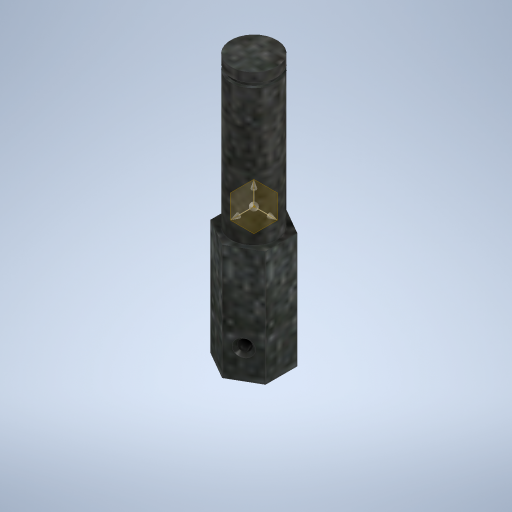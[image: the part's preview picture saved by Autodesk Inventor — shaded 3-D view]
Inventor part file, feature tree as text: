
AUTODESK INVENTOR PART (.ipt)
format: ipt  version: 2023 (Build 270158030, 158C)  size: 348,160 bytes
history: native  units: in
note: dims shown in document units (in); Inventor stores cm internally (conversion verified against a paired STEP export)
features: sketch x5, extrude x3, hole x1, revolve x1
ambient origin geometry x8: Origin, YZ Plane, XZ Plane, XY Plane, X Axis, Y Axis, Z Axis, Center Point
bodies: Solid1 (feature_tree)
feature tree (10):
  extrude  "Extrusion1"  Depth=0.7874in TaperAngle=0.0deg
  extrude  "Extrusion2"  Depth=0.1969in TaperAngle=0.0deg
  hole  "Hole1"  [1 undecoded]
  extrude  "Extrusion4"  Depth=0.1083in
  revolve  "Revolution1"  [1 undecoded]
  sketch  "Sketch1"  dims[d0=0.375in d1=0.7874in d2=0.0in]
  sketch  "Sketch2"  dims[d3=0.315in d4=0.1969in d5=0.0in]
  sketch  "Sketch4"  dims[d11=0.835in d12=0.0in d13=0.1969in]
  sketch  "Sketch5"  dims[d14=0.0787in d15=0.75in d16=0.1181in d17=0.25in d18=0.5635in d19=1.0in d20=0.8108in d21=0.1083in]
  sketch  "Sketch6"  dims[d22=0.8268in d23=0.0in d24=0.0939in d25=0.0315in d26=0.2756in d27=90.0deg]
note: 2 required parameter values undecoded (feature->parameter linkage not recoverable at this tier; creation-order binding heuristic only, values carry confidence <= 0.55)